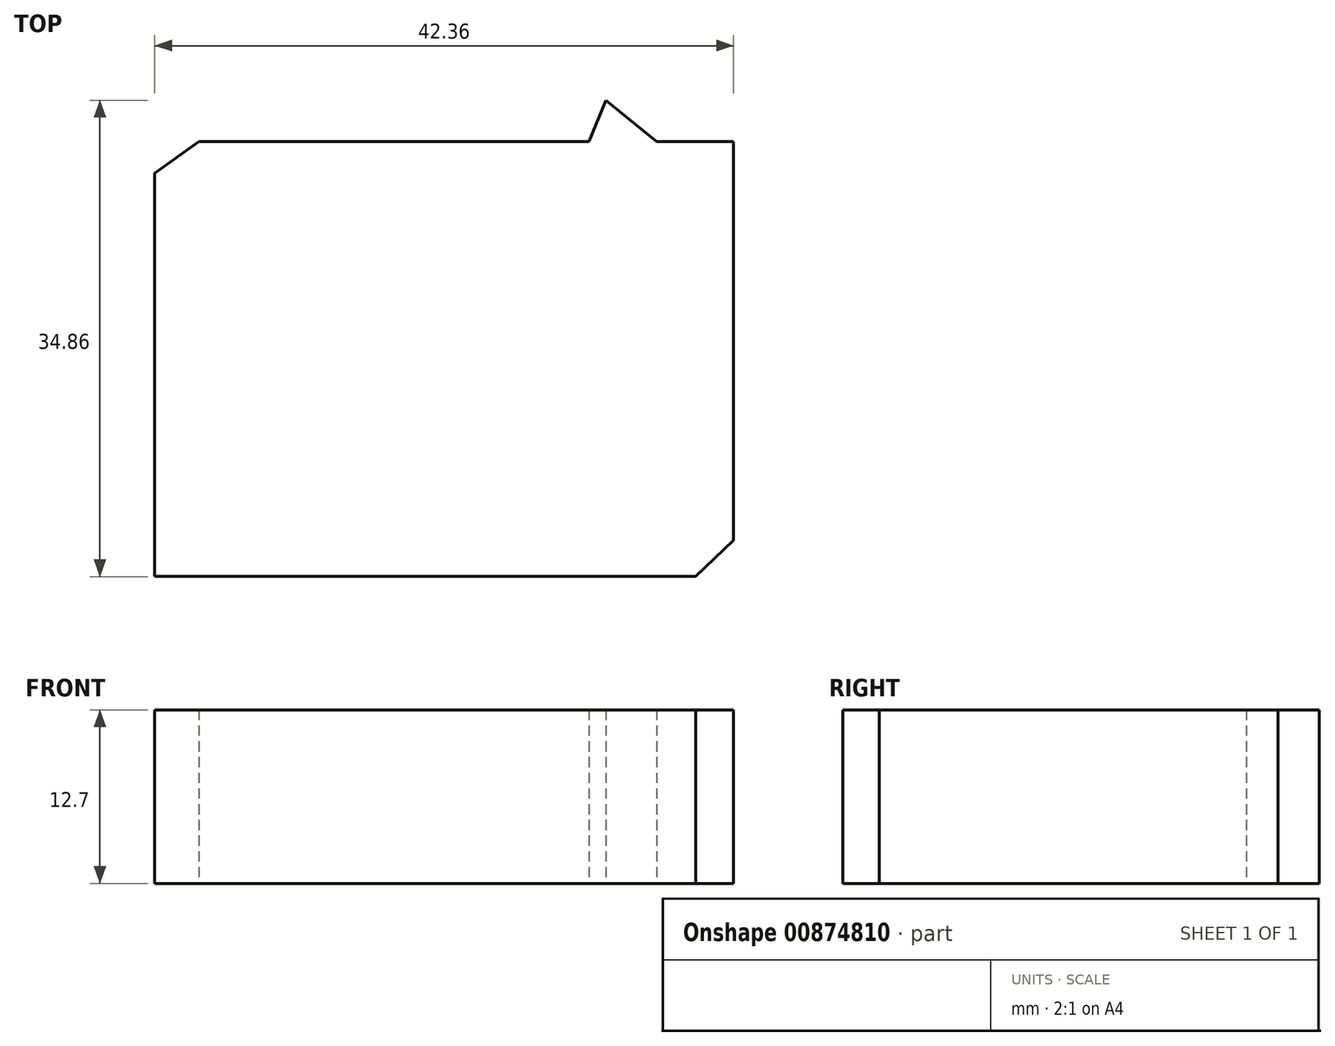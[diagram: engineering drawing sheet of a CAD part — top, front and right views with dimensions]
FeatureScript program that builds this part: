
annotation { "Feature Type Name" : "Feature", "Feature Type Description" : "" }
export const myFeature = defineFeature(function(context is Context, id is Id, definition is map)
    precondition{}
    {
        {
            var Q0;
            Q0=qCreatedBy(makeId("Top.planeOp"),FACE);
            var sketch = newSketch(context, id + "F0", { "sketchPlane" : qUnion([Q0])});
            skLineSegment(sketch, "E0.bottom", {"start": v(-20.21, 14.61) * mm, "end": v(18.9, 14.61) * mm});
            skLineSegment(sketch, "E0.top", {"start": v(-20.21, -14.56) * mm, "end": v(18.9, -14.56) * mm});
            skLineSegment(sketch, "E0.left", {"start": v(-20.21, 14.61) * mm, "end": v(-20.21, -14.56) * mm});
            skLineSegment(sketch, "E0.right", {"start": v(18.9, 14.61) * mm, "end": v(18.9, -14.56) * mm});
            skLineSegment(sketch, "E1", {"start": v(3.53, 3.14) * mm, "end": v(9.57, 17.64) * mm});
            skLineSegment(sketch, "E2", {"start": v(9.57, 17.64) * mm, "end": v(16.13, 12.29) * mm});
            skLineSegment(sketch, "E3", {"start": v(16.13, 12.29) * mm, "end": v(9.57, -5.31) * mm});
            skLineSegment(sketch, "E4", {"start": v(9.57, -5.31) * mm, "end": v(3.53, 3.14) * mm});
            skLineSegment(sketch, "E5", {"start": v(-20.21, 14.61) * mm, "end": v(-23.46, 12.29) * mm});
            skLineSegment(sketch, "E6", {"start": v(-23.46, 12.29) * mm, "end": v(-23.46, -17.22) * mm});
            skLineSegment(sketch, "E7", {"start": v(-23.46, -17.22) * mm, "end": v(-20.21, -14.56) * mm});
            skLineSegment(sketch, "E8", {"start": v(-23.46, -17.22) * mm, "end": v(16.13, -17.22) * mm});
            skLineSegment(sketch, "E9", {"start": v(16.13, -17.22) * mm, "end": v(18.9, -14.56) * mm});
            skSolve(sketch);
        }
        {
            var Q0;
            Q0 = qSketchRegion(id + "F0", true);
            extrude(context, id + "F1", {"entities" : qUnion([Q0]), "depth" : 12.7 * mm, "offsetDistance" : 25.4 * mm});
        }
    });
